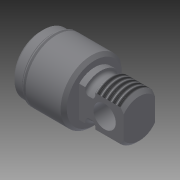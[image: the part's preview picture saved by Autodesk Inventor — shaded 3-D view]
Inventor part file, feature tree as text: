
AUTODESK INVENTOR PART (.ipt)
format: ipt  version: 2014 (Build 180170000, 170)  size: 288,256 bytes
history: native  units: in
note: dims shown in document units (in); Inventor stores cm internally (conversion verified against a paired STEP export)
features: other x91, sketch x9, revolve x7, thread x2, hole x1, extrude x1
ambient origin geometry x8: Origin, YZ Plane, XZ Plane, XY Plane, X Axis, Y Axis, Z Axis, Center Point
bodies: Solid1 (feature_tree)
feature tree (111):
  revolve  "Revolution1"  Angle=360.0deg
  hole  "Hole1"  [1 undecoded]
  revolve  "Revolution2"  [1 undecoded]
  revolve  "Revolution3"  Angle=360.0deg
  revolve  "Revolution4"  [1 undecoded]
  revolve  "Revolution5"  [1 undecoded]
  thread  "Thread1"  [1 undecoded]
  extrude  "Extrusion1"  [1 undecoded]
  revolve  "Revolution6"  [1 undecoded]
  revolve  "Revolution7"  [1 undecoded]
  thread  "Thread2"  [1 undecoded]
  other  "aa2_XY"
  other  "aa2_YZ"
  other  "aa2_ZX"
  other  "aa2_X"
  other  "aa2_Y"
  other  "aa2_Z"
  other  "aa2_Center"
  other  "mm1_XY"
  other  "mm1_YZ"
  other  "mm1_ZX"
  other  "mm1_X"
  other  "mm1_Y"
  other  "mm1_Z"
  other  "mm1_Center"
  other  "mm2_XY"
  other  "mm2_YZ"
  other  "mm2_ZX"
  other  "mm2_X"
  other  "mm2_Y"
  other  "mm2_Z"
  other  "mm2_Center"
  other  "nn1_XY"
  other  "nn1_YZ"
  other  "nn1_ZX"
  other  "nn1_X"
  other  "nn1_Y"
  other  "nn1_Z"
  other  "nn1_Center"
  other  "nn2_XY"
  other  "nn2_YZ"
  other  "nn2_ZX"
  other  "nn2_X"
  other  "nn2_Y"
  other  "nn2_Z"
  other  "nn2_Center"
  other  "p1_XY"
  other  "p1_YZ"
  other  "p1_ZX"
  other  "p1_X"
  other  "p1_Y"
  other  "p1_Z"
  other  "p1_Center"
  other  "q2_XY"
  other  "q2_YZ"
  other  "q2_ZX"
  other  "q2_X"
  other  "q2_Y"
  other  "q2_Z"
  other  "q2_Center"
  other  "r1_XY"
  other  "r1_YZ"
  other  "r1_ZX"
  other  "r1_X"
  other  "r1_Y"
  other  "r1_Z"
  other  "r1_Center"
  other  "r2_XY"
  other  "r2_YZ"
  other  "r2_ZX"
  other  "r2_X"
  other  "r2_Y"
  other  "r2_Z"
  other  "r2_Center"
  other  "rear_head_XY"
  other  "rear_head_YZ"
  other  "rear_head_ZX"
  other  "rear_head_X"
  other  "rear_head_Y"
  other  "rear_head_Z"
  other  "rear_head_Center"
  other  "to_bushing_XY"
  other  "to_bushing_YZ"
  other  "to_bushing_ZX"
  other  "to_bushing_X"
  other  "to_bushing_Y"
  other  "to_bushing_Z"
  other  "to_bushing_Center"
  other  "to_mounting_bracket_xp_XY"
  other  "to_mounting_bracket_xp_YZ"
  other  "to_mounting_bracket_xp_ZX"
  other  "to_mounting_bracket_xp_X"
  other  "to_mounting_bracket_xp_Y"
  other  "to_mounting_bracket_xp_Z"
  other  "to_mounting_bracket_xp_Center"
  other  "to_pivot_bracket_XY"
  other  "to_pivot_bracket_YZ"
  other  "to_pivot_bracket_ZX"
  other  "to_pivot_bracket_X"
  other  "to_pivot_bracket_Y"
  other  "to_pivot_bracket_Z"
  other  "to_pivot_bracket_Center"
  sketch  "Sketch_1"  dims[d0=360.0deg]
  sketch  "Sketch2"  dims[d1=0.375in d2=0.75in d3=0.435in d4=0.25in d5=90.0deg d6=0.188in d7=0.0in d8=360.0deg]
  sketch  "Sketch_6"  dims[d9=360.0deg d10=360.0deg]
  sketch  "Sketch_9"  dims[d11=360.0deg d12=0.2472in d13=0.0in]
  sketch  "Sketch_23"
  sketch  "Sketch_12"  dims[d14=0.437in d15=0.0in d16=360.0deg]
  sketch  "Sketch_13"  dims[d17=360.0deg d18=0.1686in d19=0.0in]
  sketch  "Sketch_21"
  sketch  "Sketch_17"
note: 9 required parameter values undecoded (feature->parameter linkage not recoverable at this tier; creation-order binding heuristic only, values carry confidence <= 0.55)